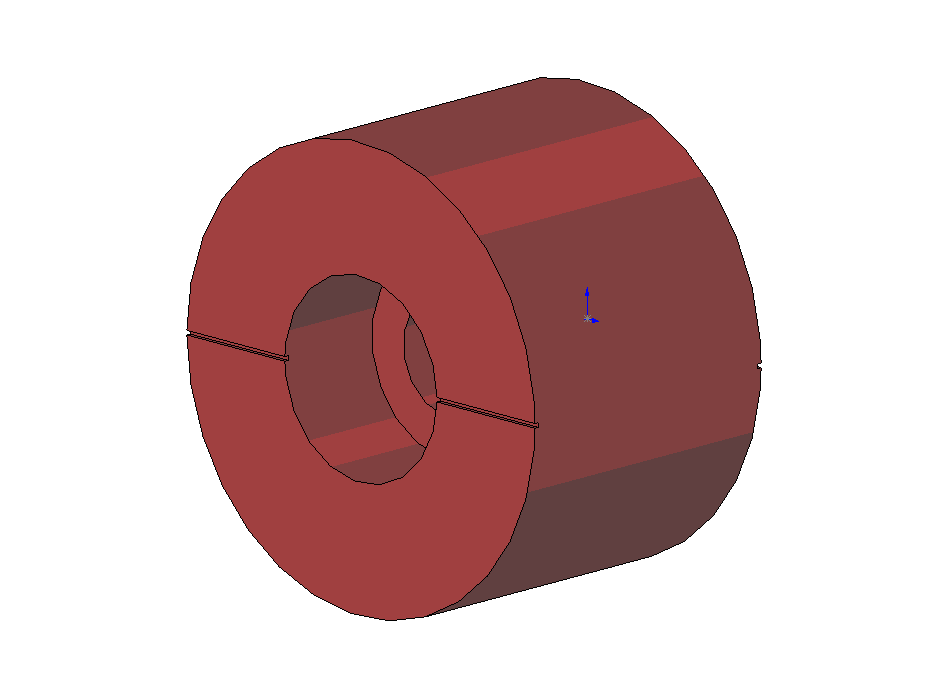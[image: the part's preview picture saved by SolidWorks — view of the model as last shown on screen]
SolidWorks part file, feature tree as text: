
SOLIDWORKS PART (.sldprt)
format: sldprt  version: not decoded by parser v0  size: 325,120 bytes
history: native  units: mm
features: sketch x5, cut_extrude x2, material x1, extrude x1, hole x1 (+12 scaffold rows collapsed)
feature tree (22):
  scaffold x12  (default folders/planes/origin — collapsed)
  material  "Material <not specified>"
  sketch  "Sketch1"  dims[D1=25.4mm]
  extrude  "Base-Extrude"  Depth=16.5mm
  hole  "CBORE for 1/4 Socket Head Cap Screw1"  Diameter=6.5278mm Depth=16.5mm
  sketch  "Sketch3"
  sketch  "Sketch2"  dims[hole-wizard template sketch: 41 standard entries collapsed; hole parameters kept: c12.Thru Hole Dia.=6.5278mm c12.Thru Hole Depth=16.5mm c12.C'Bore Dia.=11.1125mm c12.C'Bore Depth=6.35mm]
  sketch  "Sketch4"  dims[D1=0.25mm]
  cut_extrude  "Vent Groove Front"  Depth=0.25mm
  sketch  "Sketch5"  dims[D1=0.25mm]
  cut_extrude  "Vent Groove Back"  Depth=0.25mm
decode coverage: 8 of 9 modeling features carry decoded parameters
note: ~ marks probable driven/reference dimensions
note: suppression state not decoded; provenance and decode notes live in map.json
